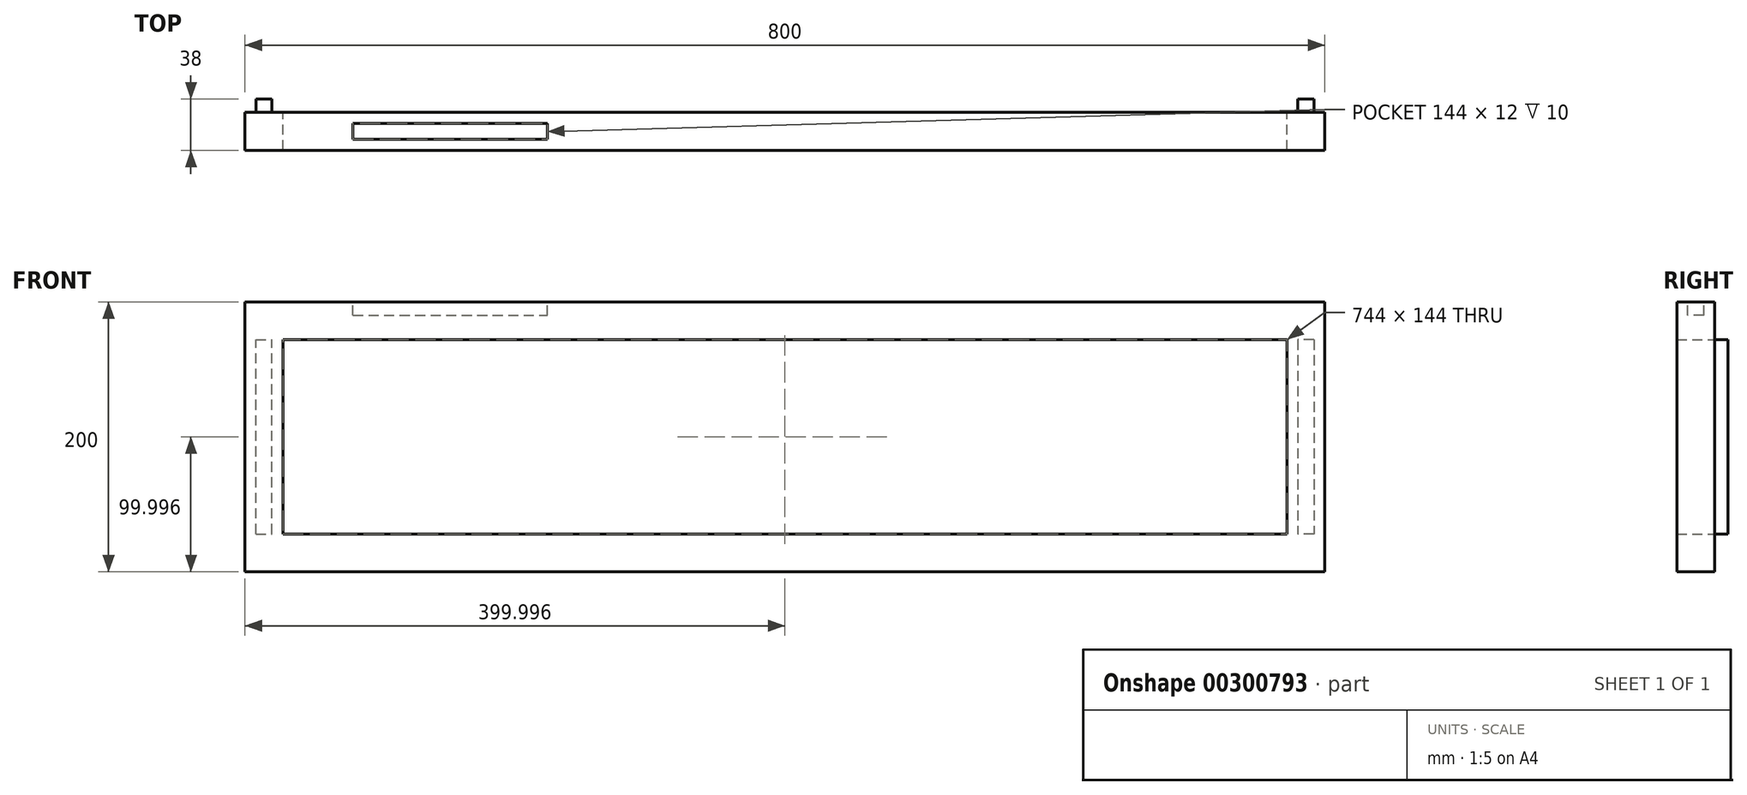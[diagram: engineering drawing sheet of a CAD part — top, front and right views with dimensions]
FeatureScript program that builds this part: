
annotation { "Feature Type Name" : "Feature", "Feature Type Description" : "" }
export const myFeature = defineFeature(function(context is Context, id is Id, definition is map)
    precondition{}
    {
        {
            var Q0;
            Q0=qCreatedBy(makeId("Front.planeOp"),FACE);
            var sketch = newSketch(context, id + "F0", { "sketchPlane" : qUnion([Q0])});
            skLineSegment(sketch, "E0.bottom", {"start": v(-981.05, -103.42) * mm, "end": v(1018.95, -103.42) * mm});
            skLineSegment(sketch, "E0.top", {"start": v(-981.05, -603.42) * mm, "end": v(1018.95, -603.42) * mm});
            skLineSegment(sketch, "E0.left", {"start": v(-981.05, -103.42) * mm, "end": v(-981.05, -603.42) * mm});
            skLineSegment(sketch, "E0.right", {"start": v(1018.95, -103.42) * mm, "end": v(1018.95, -603.42) * mm});
            skLineSegment(sketch, "E1.bottom", {"start": v(-911.05, -173.42) * mm, "end": v(948.95, -173.42) * mm});
            skLineSegment(sketch, "E1.top", {"start": v(-911.05, -533.42) * mm, "end": v(948.95, -533.42) * mm});
            skLineSegment(sketch, "E1.left", {"start": v(-911.05, -173.42) * mm, "end": v(-911.05, -533.42) * mm});
            skLineSegment(sketch, "E1.right", {"start": v(948.95, -173.42) * mm, "end": v(948.95, -533.42) * mm});
            skPoint(sketch, "E2", {"position": v(-911.05, -533.42) * mm});
            skSolve(sketch);
        }
        {
            var Q0;
            Q0=makeQuery(id+"F0.imprint","IMPRINT",FACE,{"disambiguationData":[TD([[makeQuery(id+"F0.imprint","IMPRINT",EDGE,{"derivedFrom":sQuery(id+"F0.wireOp",EDGE,"E0.bottom")}),-1.0]])]});
            extrude(context, id + "F1", {"entities" : qUnion([Q0]), "depth" : 70 * mm});
        }
        {
            var Q0;
            Q0=makeQuery(id+"F1.opExtrude","CAP_FACE",FACE,{"disambiguationData":[OSD([sQuery(id+"F0.wireOp",EDGE,"E0.bottom"),sQuery(id+"F0.wireOp",EDGE,"E0.top"),sQuery(id+"F0.wireOp",EDGE,"E0.left"),sQuery(id+"F0.wireOp",EDGE,"E0.right"),sQuery(id+"F0.wireOp",EDGE,"E1.bottom"),sQuery(id+"F0.wireOp",EDGE,"E1.top"),sQuery(id+"F0.wireOp",EDGE,"E1.left"),sQuery(id+"F0.wireOp",EDGE,"E1.right")])],"isStart":true});
            var sketch = newSketch(context, id + "F2", { "sketchPlane" : qUnion([Q0])});
            skLineSegment(sketch, "E3.bottom", {"start": v(-998.95, -173.42) * mm, "end": v(-968.95, -173.42) * mm});
            skLineSegment(sketch, "E3.top", {"start": v(-998.95, -533.42) * mm, "end": v(-968.95, -533.42) * mm});
            skLineSegment(sketch, "E3.left", {"start": v(-998.95, -173.42) * mm, "end": v(-998.95, -533.42) * mm});
            skLineSegment(sketch, "E3.right", {"start": v(-968.95, -173.42) * mm, "end": v(-968.95, -533.42) * mm});
            skLineSegment(sketch, "E4.bottom", {"start": v(931.05, -173.42) * mm, "end": v(961.05, -173.42) * mm});
            skLineSegment(sketch, "E4.top", {"start": v(931.05, -533.42) * mm, "end": v(961.05, -533.42) * mm});
            skLineSegment(sketch, "E4.left", {"start": v(931.05, -173.42) * mm, "end": v(931.05, -533.42) * mm});
            skLineSegment(sketch, "E4.right", {"start": v(961.05, -173.42) * mm, "end": v(961.05, -533.42) * mm});
            skSolve(sketch);
        }
        {
            var Q0;
            Q0=makeQuery(id+"F2.imprint","IMPRINT",FACE,{"disambiguationData":[TD([[makeQuery(id+"F2.imprint","IMPRINT",EDGE,{"derivedFrom":sQuery(id+"F2.wireOp",EDGE,"E4.bottom")}),-1.0]])]});
            extrude(context, id + "F3", {"entities" : qUnion([Q0]), "oppositeDirection" : true, "depth" : 25 * mm});
        }
        {
            var Q0;
            Q0=qSketchRegion(id+"F2",true);
            extrude(context, id + "F4", {"entities" : qUnion([Q0]), "operationType" : NewBodyOperationType.ADD, "depth" : 25 * mm});
        }
        {
            var Q0;
            Q0=makeQuery(id+"F1.opExtrude","SWEPT_FACE",FACE,{"disambiguationData":[OSD([sQuery(id+"F0.wireOp",EDGE,"E0.bottom")])]});
            var sketch = newSketch(context, id + "F5", { "sketchPlane" : qUnion([Q0])});
            skLineSegment(sketch, "E5.bottom", {"start": v(-781.05, -20) * mm, "end": v(-421.05, -20) * mm});
            skLineSegment(sketch, "E5.top", {"start": v(-781.05, -50) * mm, "end": v(-421.05, -50) * mm});
            skLineSegment(sketch, "E5.left", {"start": v(-781.05, -20) * mm, "end": v(-781.05, -50) * mm});
            skLineSegment(sketch, "E5.right", {"start": v(-421.05, -20) * mm, "end": v(-421.05, -50) * mm});
            skSolve(sketch);
        }
        {
            var Q0;
            Q0=makeQuery(id+"F5.imprint","IMPRINT",FACE,{"disambiguationData":[TD([[makeQuery(id+"F5.imprint","IMPRINT",EDGE,{"derivedFrom":sQuery(id+"F5.wireOp",EDGE,"E5.bottom")}),-1.0]])]});
            extrude(context, id + "F6", {"entities" : qUnion([Q0]), "operationType" : NewBodyOperationType.REMOVE, "oppositeDirection" : true, "depth" : 25 * mm});
        }
        {
            var Q0;
            Q0=makeQuery(id+"F1.opExtrude","SWEPT_BODY",BODY,{"disambiguationData":[OSD([sQuery(id+"F0.wireOp",EDGE,"E0.bottom"),sQuery(id+"F0.wireOp",EDGE,"E0.top"),sQuery(id+"F0.wireOp",EDGE,"E0.left"),sQuery(id+"F0.wireOp",EDGE,"E0.right"),sQuery(id+"F0.wireOp",EDGE,"E1.bottom"),sQuery(id+"F0.wireOp",EDGE,"E1.top"),sQuery(id+"F0.wireOp",EDGE,"E1.left"),sQuery(id+"F0.wireOp",EDGE,"E1.right")])]});
            var Q1;
            Q1=makeQuery(id+"F1.opExtrude","CAP_EDGE",EDGE,{"disambiguationData":[OSD([sQuery(id+"F0.wireOp",EDGE,"E0.bottom")])],"isStart":false});
            var Q2;
            Q2=makeQuery(id+"F1.opExtrude","CAP_VERTEX",VERTEX,{"disambiguationData":[OSD([sQuery(id+"F0.wireOp",EDGE,"E0.top"),sQuery(id+"F0.wireOp",EDGE,"E0.right")])],"isStart":false});
            transform(context, id + "F7", {"entities" : qUnion([Q0]), "transformType" : TransformType.SCALE_UNIFORMLY, "scale" : 0.4, "scalePoint" : qUnion([Q2]), "makeCopy" : false});
        }
    });
